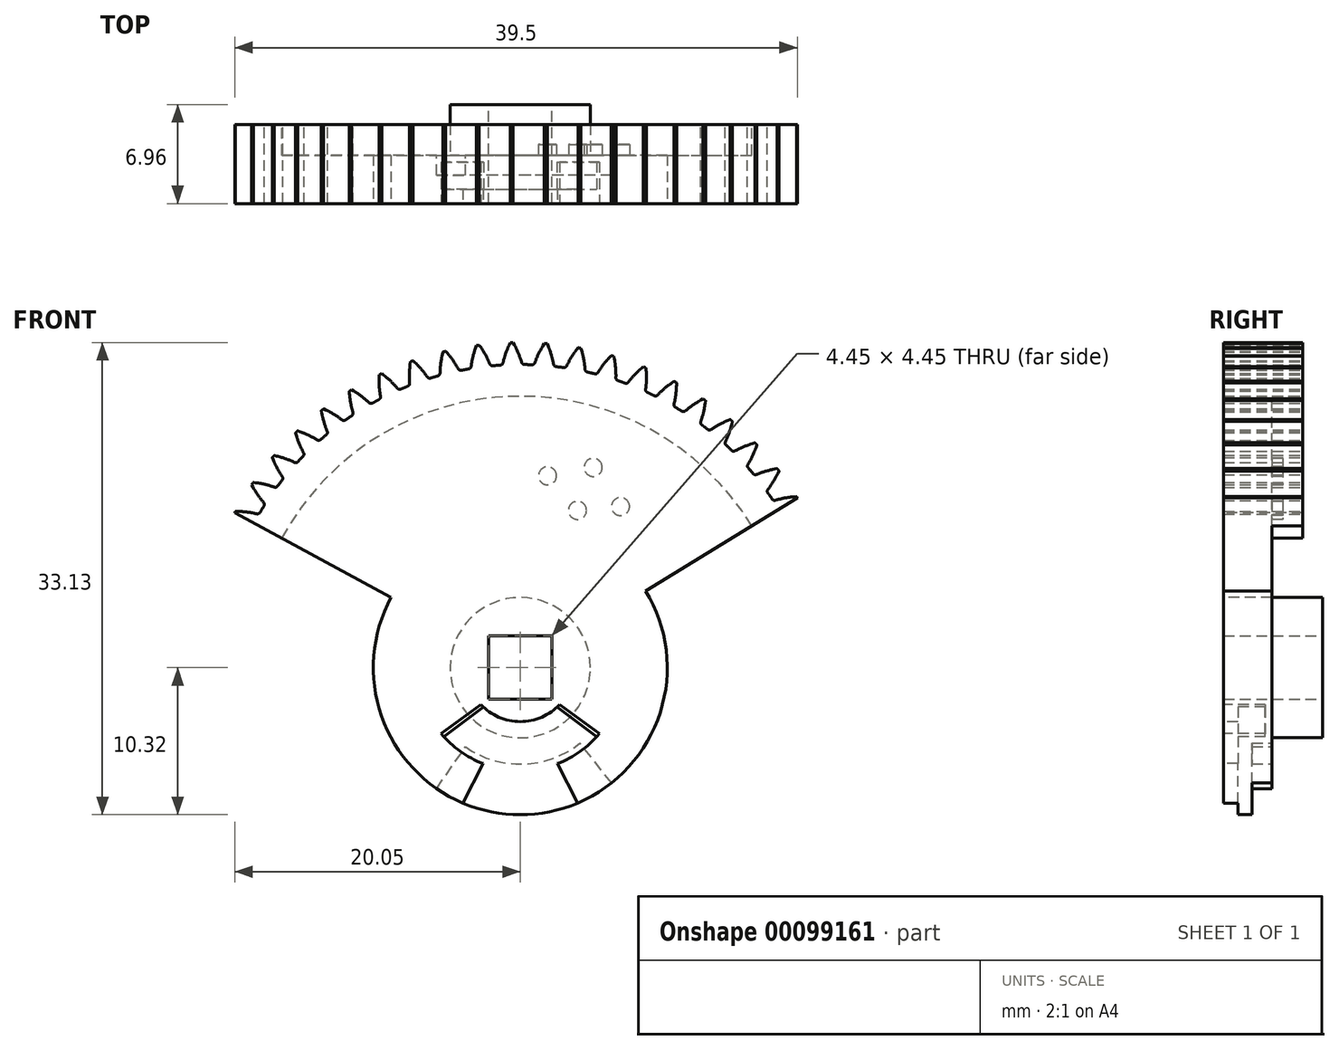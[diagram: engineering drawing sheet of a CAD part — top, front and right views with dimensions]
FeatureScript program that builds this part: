
annotation { "Feature Type Name" : "Feature", "Feature Type Description" : "" }
export const myFeature = defineFeature(function(context is Context, id is Id, definition is map)
    precondition{}
    {
        {
            assignVariable(context, id + "F0", {"name" : "Teeth", "anyValue" : 60});
        }
        {
            var Q0;
            Q0=qCreatedBy(makeId("Front.planeOp"),FACE);
            var sketch = newSketch(context, id + "F1", { "sketchPlane" : qUnion([Q0])});
            skCircle(sketch, "E0", {"center": v(0, 0) * mm, "radius": 20.77 * mm, "construction": true});
            skLineSegment(sketch, "E1", {"start": v(0, 0) * mm, "end": v(-0.74, 20.75) * mm, "construction": true});
            skLineSegment(sketch, "E2", {"start": v(0, 0) * mm, "end": v(-1.69, 20.7) * mm, "construction": true});
            skLineSegment(sketch, "E3", {"start": v(0, 0) * mm, "end": v(-2.64, 20.6) * mm, "construction": true});
            skLineSegment(sketch, "E4", {"start": v(-2.64, 20.6) * mm, "end": v(0.2, 20.96) * mm, "construction": true});
            skLineSegment(sketch, "E5", {"start": v(0, 0) * mm, "end": v(-3.58, 20.45) * mm, "construction": true});
            skLineSegment(sketch, "E6", {"start": v(-3.58, 20.45) * mm, "end": v(0.17, 21.11) * mm, "construction": true});
            skLineSegment(sketch, "E7", {"start": v(-2.64, 20.6) * mm, "end": v(-1.69, 20.7) * mm, "construction": true});
            skLineSegment(sketch, "E8", {"start": v(-3.58, 20.45) * mm, "end": v(-2.64, 20.6) * mm, "construction": true});
            skLineSegment(sketch, "E9", {"start": v(-2.64, 20.6) * mm, "end": v(-0.74, 20.75) * mm, "construction": true});
            skLineSegment(sketch, "E10", {"start": v(-3.58, 20.45) * mm, "end": v(-0.74, 20.75) * mm, "construction": true});
            skLineSegment(sketch, "E11", {"start": v(0, 0) * mm, "end": v(-6.35, 19.77) * mm, "construction": true});
            skLineSegment(sketch, "E12", {"start": v(-6.35, 19.77) * mm, "end": v(-0.03, 21.8) * mm, "construction": true});
            skLineSegment(sketch, "E13", {"start": v(0, 0) * mm, "end": v(-5.44, 20.04) * mm, "construction": true});
            skLineSegment(sketch, "E14", {"start": v(-5.44, 20.04) * mm, "end": v(0.06, 21.53) * mm, "construction": true});
            skLineSegment(sketch, "E15", {"start": v(0, 0) * mm, "end": v(-4.51, 20.27) * mm, "construction": true});
            skLineSegment(sketch, "E16", {"start": v(-4.51, 20.27) * mm, "end": v(0.13, 21.3) * mm, "construction": true});
            skLineSegment(sketch, "E17", {"start": v(-4.51, 20.27) * mm, "end": v(-3.58, 20.45) * mm, "construction": true});
            skLineSegment(sketch, "E18", {"start": v(-4.51, 20.27) * mm, "end": v(-5.44, 20.04) * mm, "construction": true});
            skLineSegment(sketch, "E19", {"start": v(-5.44, 20.04) * mm, "end": v(-6.35, 19.77) * mm, "construction": true});
            skLineSegment(sketch, "E20", {"start": v(-4.51, 20.27) * mm, "end": v(-0.74, 20.75) * mm, "construction": true});
            skLineSegment(sketch, "E21", {"start": v(-5.44, 20.04) * mm, "end": v(-0.74, 20.75) * mm, "construction": true});
            skLineSegment(sketch, "E22", {"start": v(-6.35, 19.77) * mm, "end": v(-0.74, 20.75) * mm, "construction": true});
            skLineSegment(sketch, "E23", {"start": v(0, 0) * mm, "end": v(-8.13, 19.1) * mm, "construction": true});
            skLineSegment(sketch, "E24", {"start": v(-8.13, 19.1) * mm, "end": v(-0.3, 22.44) * mm, "construction": true});
            skLineSegment(sketch, "E25", {"start": v(0, 0) * mm, "end": v(-9, 18.71) * mm, "construction": true});
            skLineSegment(sketch, "E26", {"start": v(-9, 18.71) * mm, "end": v(-0.5, 22.8) * mm, "construction": true});
            skLineSegment(sketch, "E27", {"start": v(0, 0) * mm, "end": v(-9.85, 18.28) * mm, "construction": true});
            skLineSegment(sketch, "E28", {"start": v(0, 0) * mm, "end": v(-7.25, 19.46) * mm, "construction": true});
            skLineSegment(sketch, "E29", {"start": v(-7.25, 19.46) * mm, "end": v(-0.15, 22.1) * mm, "construction": true});
            skLineSegment(sketch, "E30", {"start": v(-6.35, 19.77) * mm, "end": v(-7.25, 19.46) * mm, "construction": true});
            skLineSegment(sketch, "E31", {"start": v(-7.25, 19.46) * mm, "end": v(-8.13, 19.1) * mm, "construction": true});
            skLineSegment(sketch, "E32", {"start": v(-8.13, 19.1) * mm, "end": v(-9, 18.71) * mm, "construction": true});
            skLineSegment(sketch, "E33", {"start": v(-9, 18.71) * mm, "end": v(-9.85, 18.28) * mm, "construction": true});
            skLineSegment(sketch, "E34", {"start": v(-0.74, 20.75) * mm, "end": v(-7.25, 19.46) * mm, "construction": true});
            skLineSegment(sketch, "E35", {"start": v(-0.74, 20.75) * mm, "end": v(-8.13, 19.1) * mm, "construction": true});
            skLineSegment(sketch, "E36", {"start": v(-0.74, 20.75) * mm, "end": v(-9, 18.71) * mm, "construction": true});
            skLineSegment(sketch, "E37", {"start": v(-0.74, 20.75) * mm, "end": v(-9.85, 18.28) * mm, "construction": true});
            skCircle(sketch, "E38", {"center": v(0, 0) * mm, "radius": 22.1 * mm, "construction": true});
            skCircle(sketch, "E39", {"center": v(0, 0) * mm, "radius": 22.81 * mm});
            skPoint(sketch, "E40", {"position": v(0, 22.1) * mm});
            skLineSegment(sketch, "E41", {"start": v(0, 0) * mm, "end": v(-0.23, 8.6) * mm, "construction": true});
            skPoint(sketch, "E42.MirrorP", {"position": v(-1.16, 22.07) * mm});
            skLineSegment(sketch, "E43", {"start": v(-1.16, 22.07) * mm, "end": v(0, 0) * mm, "construction": true});
            skLineSegment(sketch, "E44", {"start": v(0, 0) * mm, "end": v(0, 22.1) * mm, "construction": true});
            skLineSegment(sketch, "E45", {"start": v(-1.69, 20.7) * mm, "end": v(-0.74, 20.75) * mm, "construction": true});
            skLineSegment(sketch, "E46", {"start": v(0.2, 20.96) * mm, "end": v(0.17, 21.11) * mm, "construction": true});
            skLineSegment(sketch, "E47", {"start": v(0, 0) * mm, "end": v(0, 10.19) * mm, "construction": true});
            skCircle(sketch, "E48", {"center": v(0, 0) * mm, "radius": 21.27 * mm});
            skSolve(sketch);
        }
        {
            var Q0;
            Q0=qCreatedBy(makeId("Front.planeOp"),FACE);
            var sketch = newSketch(context, id + "F2", { "sketchPlane" : qUnion([Q0])});
            skCircle(sketch, "E49.0", {"center": v(0, 0) * mm, "radius": 22.1 * mm, "construction": true});
            skPoint(sketch, "E50.0", {"position": v(-0.5, 22.8) * mm});
            skPoint(sketch, "E50.1", {"position": v(-0.3, 22.44) * mm});
            skPoint(sketch, "E50.2", {"position": v(-0.15, 22.1) * mm});
            skPoint(sketch, "E50.3", {"position": v(-0.03, 21.8) * mm});
            skPoint(sketch, "E50.4", {"position": v(0.06, 21.53) * mm});
            skPoint(sketch, "E50.6", {"position": v(0.17, 21.11) * mm});
            skPoint(sketch, "E50.7", {"position": v(0.2, 20.96) * mm});
            skPoint(sketch, "E50.8", {"position": v(0.13, 21.3) * mm});
            skLineSegment(sketch, "E51.0", {"start": v(0, 0) * mm, "end": v(-0.23, 8.6) * mm, "construction": true});
            skFitSpline(sketch, "E52", {"points": [v(-0.5, 22.8) * mm, v(-0.3, 22.44) * mm, v(-0.15, 22.1) * mm, v(-0.03, 21.8) * mm, v(0.06, 21.53) * mm, v(0.13, 21.3) * mm, v(0.17, 21.11) * mm, v(0.2, 20.96) * mm], "startDerivative": vector(3.27, -6.28) * mm, "endDerivative": vector(0.74, -4.25) * mm});
            skFitSpline(sketch, "E53.MirrorCS", {"points": [v(-0.7, 22.8) * mm, v(-0.87, 22.43) * mm, v(-1, 22.08) * mm, v(-1.11, 21.77) * mm, v(-1.19, 21.5) * mm, v(-1.24, 21.27) * mm, v(-1.28, 21.07) * mm, v(-1.3, 20.92) * mm], "startDerivative": vector(-2.94, -6.45) * mm, "endDerivative": vector(-0.51, -4.28) * mm});
            skCircle(sketch, "E54", {"center": v(0, 0) * mm, "radius": 2.22 * mm});
            skCircle(sketch, "E55.0", {"center": v(0, 0) * mm, "radius": 21.27 * mm});
            skArc(sketch, "E56", {"start": v(-0.5, 22.8) * mm, "mid": v(-0.6, 22.8) * mm, "end": v(-0.7, 22.8) * mm});
            skLineSegment(sketch, "E57", {"start": v(-1.3, 20.92) * mm, "end": v(0, 0) * mm});
            skLineSegment(sketch, "E58", {"start": v(0, 0) * mm, "end": v(0.2, 20.96) * mm});
            skSolve(sketch);
        }
        {
            var Q0;
            {var subQ1=sQuery(id+"F2.wireOp",EDGE,"E52");var subQ9=sQuery(id+"F2.wireOp",EDGE,"rA0usyOi-Jm6w-jZNR-JSDv-ujEcH4bsm2Ol");var subQ11=makeQuery(id+"F2.imprint","INTERSECT",VERTEX,{"derivedFrom":[subQ1,subQ9]});Q0=makeQuery(id+"F2.imprint","IMPRINT",FACE,{"disambiguationData":[TD([[makeQuery(id+"F2.imprint","IMPRINT",EDGE,{"disambiguationData":[TD([[subQ11,1.0]])],"derivedFrom":subQ1}),-1.0]])]});}
            var Q1;
            {var subQ0=sQuery(id+"F2.wireOp",EDGE,"QqPcIgQ4-TZE6-73E5-WQaq-ugCT5JtziKyn");var subQ1=sQuery(id+"F2.wireOp",EDGE,"90be38e0-c88f-493d-85a8-1201295b9109.0");var subQ2=makeQuery(id+"F2.imprint","INTERSECT",VERTEX,{"derivedFrom":[subQ1,subQ0]});Q1=makeQuery(id+"F2.imprint","IMPRINT",FACE,{"disambiguationData":[TD([[makeQuery(id+"F2.imprint","IMPRINT",EDGE,{"disambiguationData":[TD([[subQ2,1.0]])],"derivedFrom":subQ1}),1.0]])]});}
            var Q2;
            {var subQ0=sQuery(id+"F2.wireOp",EDGE,"QqPcIgQ4-TZE6-73E5-WQaq-ugCT5JtziKyn");var subQ1=sQuery(id+"F2.wireOp",EDGE,"90be38e0-c88f-493d-85a8-1201295b9109.0");var subQ2=makeQuery(id+"F2.imprint","INTERSECT",VERTEX,{"derivedFrom":[subQ1,subQ0]});Q2=makeQuery(id+"F2.imprint","IMPRINT",FACE,{"disambiguationData":[TD([[makeQuery(id+"F2.imprint","IMPRINT",EDGE,{"disambiguationData":[TD([[subQ2,-1.0]])],"derivedFrom":subQ1}),1.0]])]});}
            var Q3;
            {var subQ1=sQuery(id+"F2.wireOp",EDGE,"E52");var subQ8=sQuery(id+"F2.wireOp",EDGE,"b861a5ab-cd51-40f1-92ab-cea0f5fe0d4d.1");var subQ11=makeQuery(id+"F2.imprint","INTERSECT",VERTEX,{"derivedFrom":[subQ1,subQ8]});Q3=makeQuery(id+"F2.imprint","IMPRINT",FACE,{"disambiguationData":[TD([[makeQuery(id+"F2.imprint","IMPRINT",EDGE,{"disambiguationData":[TD([[subQ11,1.0]])],"derivedFrom":subQ1}),-1.0]])]});}
            var Q4;
            {var subQ0=sQuery(id+"F2.wireOp",EDGE,"b861a5ab-cd51-40f1-92ab-cea0f5fe0d4d.0");var subQ1=sQuery(id+"F2.wireOp",EDGE,"E54");var subQ2=makeQuery(id+"F2.imprint","INTERSECT",VERTEX,{"derivedFrom":[subQ1,subQ0]});Q4=makeQuery(id+"F2.imprint","IMPRINT",FACE,{"disambiguationData":[TD([[makeQuery(id+"F2.imprint","IMPRINT",EDGE,{"disambiguationData":[TD([[subQ2,-1.0]])],"derivedFrom":subQ1}),-1.0]])]});}
            var Q5;
            {var subQ0=sQuery(id+"F2.wireOp",EDGE,"b861a5ab-cd51-40f1-92ab-cea0f5fe0d4d.0");var subQ1=sQuery(id+"F2.wireOp",EDGE,"E54");var subQ2=makeQuery(id+"F2.imprint","INTERSECT",VERTEX,{"derivedFrom":[subQ1,subQ0]});Q5=makeQuery(id+"F2.imprint","IMPRINT",FACE,{"disambiguationData":[TD([[makeQuery(id+"F2.imprint","IMPRINT",EDGE,{"disambiguationData":[TD([[subQ2,1.0]])],"derivedFrom":subQ1}),-1.0]])]});}
            extrude(context, id + "F3", {"entities" : qUnion([Q0, Q1, Q2, Q3, Q4, Q5]), "depth" : 5.56 * mm});
        }
        {
            var Q0;
            Q0=makeQuery(id+"F3.opExtrude","SWEPT_EDGE",EDGE,{"disambiguationData":[OSD([sQuery(id+"F2.wireOp",EDGE,"b861a5ab-cd51-40f1-92ab-cea0f5fe0d4d.1"),sQuery(id+"F2.wireOp",EDGE,"E55.0")])]});
            var Q1;
            Q1=makeQuery(id+"F3.opExtrude","SWEPT_EDGE",EDGE,{"disambiguationData":[OSD([sQuery(id+"F2.wireOp",EDGE,"b861a5ab-cd51-40f1-92ab-cea0f5fe0d4d.0"),sQuery(id+"F2.wireOp",EDGE,"E55.0")])]});
            fillet(context, id + "F4", {"entities" : qUnion([Q0, Q1]), "radius" : 0.2 * mm, "tangentPropagation" : true, "allowEdgeOverflow" : false});
        }
        {
            var Q0;
            Q0=makeQuery(id+"F4.opFillet","BLEND_FACE",FACE,{"disambiguationData":[OSD([sQuery(id+"F2.wireOp",EDGE,"E55.0"),sQuery(id+"F2.wireOp",EDGE,"E57")])]});
            var Q1;
            Q1=makeQuery(id+"F3.opExtrude","SWEPT_FACE",FACE,{"disambiguationData":[OSD([sQuery(id+"F2.wireOp",EDGE,"E57")])]});
            var Q2;
            Q2=makeQuery(id+"F3.opExtrude","SWEPT_FACE",FACE,{"disambiguationData":[OSD([sQuery(id+"F2.wireOp",EDGE,"E53.MirrorCS")])]});
            var Q3;
            Q3=makeQuery(id+"F3.opExtrude","SWEPT_FACE",FACE,{"disambiguationData":[OSD([sQuery(id+"F2.wireOp",EDGE,"E56")])]});
            var Q4;
            Q4=makeQuery(id+"F3.opExtrude","SWEPT_FACE",FACE,{"disambiguationData":[OSD([sQuery(id+"F2.wireOp",EDGE,"E52")])]});
            var Q5;
            Q5=makeQuery(id+"F3.opExtrude","SWEPT_FACE",FACE,{"disambiguationData":[OSD([sQuery(id+"F2.wireOp",EDGE,"E58")])]});
            var Q6;
            Q6=makeQuery(id+"F4.opFillet","BLEND_FACE",FACE,{"disambiguationData":[OSD([sQuery(id+"F2.wireOp",EDGE,"E55.0"),sQuery(id+"F2.wireOp",EDGE,"E58")])]});
            var Q7;
            Q7=makeQuery(id+"F3.opExtrude","SWEPT_FACE",FACE,{"disambiguationData":[OSD([sQuery(id+"F2.wireOp",EDGE,"E55.0")])]});
            circularPattern(context, id + "F5", {"faces" : qUnion([Q0, Q1, Q2, Q3, Q4, Q5, Q6]), "axis" : qUnion([Q7]), "angle" : 360 * degree, "instanceCount" : round(getVariable(context, 'Teeth')), "equalSpace" : true, "patternType" : PatternType.FACE});
        }
        {
            var Q0;
            Q0=makeQuery(id+"F3.opExtrude","CAP_FACE",FACE,{"disambiguationData":[OSD([sQuery(id+"F2.wireOp",EDGE,"E52"),sQuery(id+"F2.wireOp",EDGE,"E53.MirrorCS"),sQuery(id+"F2.wireOp",EDGE,"E54"),sQuery(id+"F2.wireOp",EDGE,"E55.0"),sQuery(id+"F2.wireOp",EDGE,"E56")])],"isStart":false});
            var sketch = newSketch(context, id + "F6", { "sketchPlane" : qUnion([Q0])});
            skLineSegment(sketch, "E59", {"start": v(-9.07, 4.92) * mm, "end": v(-20.05, 10.88) * mm});
            skLineSegment(sketch, "E60", {"start": v(-25.13, -0.66) * mm, "end": v(29.24, 0.77) * mm, "construction": true});
            skLineSegment(sketch, "E61", {"start": v(0, 0) * mm, "end": v(-0.25, 9.5) * mm, "construction": true});
            skLineSegment(sketch, "E62.MirrorCS", {"start": v(8.8, 5.4) * mm, "end": v(19.45, 11.92) * mm});
            skArc(sketch, "E63", {"start": v(-9.07, 4.92) * mm, "mid": v(0.27, -10.32) * mm, "end": v(8.8, 5.4) * mm});
            skArc(sketch, "E64", {"start": v(-20.05, 10.88) * mm, "mid": v(0.6, -22.8) * mm, "end": v(19.45, 11.92) * mm});
            skSolve(sketch);
        }
        {
            var Q0;
            Q0 = qSketchRegion(id + "F6", true);
            extrude(context, id + "F7", {"entities" : qUnion([Q0]), "operationType" : NewBodyOperationType.REMOVE, "oppositeDirection" : true, "depth" : 25.4 * mm});
        }
        {
            var Q0;
            Q0=makeQuery(id+"F3.opExtrude","CAP_FACE",FACE,{"disambiguationData":[OSD([sQuery(id+"F2.wireOp",EDGE,"E52"),sQuery(id+"F2.wireOp",EDGE,"E53.MirrorCS"),sQuery(id+"F2.wireOp",EDGE,"E54"),sQuery(id+"F2.wireOp",EDGE,"E55.0"),sQuery(id+"F2.wireOp",EDGE,"E56")])],"isStart":false});
            var sketch = newSketch(context, id + "F8", { "sketchPlane" : qUnion([Q0])});
            skArc(sketch, "E65", {"start": v(-2.77, -2.58) * mm, "mid": v(-1.51, -3.47) * mm, "end": v(0, -3.78) * mm});
            skLineSegment(sketch, "E66", {"start": v(0, -3.78) * mm, "end": v(0, -10.32) * mm, "construction": true});
            skLineSegment(sketch, "E67", {"start": v(-4.03, -9.5) * mm, "end": v(-2.62, -6.74) * mm});
            skLineSegment(sketch, "E68", {"start": v(0, -4.63) * mm, "end": v(-5.54, -4.63) * mm, "construction": true});
            skArc(sketch, "E69", {"start": v(-5.54, -4.63) * mm, "mid": v(-4.21, -5.87) * mm, "end": v(-2.62, -6.74) * mm});
            skLineSegment(sketch, "E70", {"start": v(-5.54, -4.63) * mm, "end": v(-2.77, -2.58) * mm});
            skArc(sketch, "E71", {"start": v(-4.03, -9.5) * mm, "mid": v(-2.06, -10.11) * mm, "end": v(0, -10.32) * mm});
            skArc(sketch, "E72.MirrorCS", {"start": v(2.77, -2.58) * mm, "mid": v(1.51, -3.47) * mm, "end": v(0, -3.78) * mm});
            skLineSegment(sketch, "E73.MirrorCS", {"start": v(5.54, -4.63) * mm, "end": v(2.77, -2.58) * mm});
            skArc(sketch, "E74.MirrorCS", {"start": v(5.54, -4.63) * mm, "mid": v(4.21, -5.87) * mm, "end": v(2.62, -6.74) * mm});
            skLineSegment(sketch, "E75.MirrorCS", {"start": v(4.03, -9.5) * mm, "end": v(2.62, -6.74) * mm});
            skArc(sketch, "E76.MirrorCS", {"start": v(4.03, -9.5) * mm, "mid": v(2.06, -10.11) * mm, "end": v(0, -10.32) * mm});
            skSolve(sketch);
        }
        {
            var Q0;
            Q0 = qSketchRegion(id + "F8", true);
            extrude(context, id + "F9", {"entities" : qUnion([Q0]), "operationType" : NewBodyOperationType.REMOVE, "flatOperationType" : FlatOperationType.REMOVE, "oppositeDirection" : true, "offsetDistance" : 25.4 * mm, "depth" : 1.02 * mm, "domain" : OperationDomain.MODEL});
        }
        {
            var Q0;
            Q0=makeQuery(id+"F9.boolean.opBoolean","COPY",FACE,{"derivedFrom":makeQuery(id+"F9.opExtrude","CAP_FACE",FACE,{"disambiguationData":[OSD([sQuery(id+"F8.wireOp",EDGE,"7rp70U2j-1LJA-0Fld-UV0Z-6pLJ0CQ2ZY8P"),sQuery(id+"F8.wireOp",EDGE,"ceQvra0M-UReR-jHEd-x8fO-Yybck840S4PW"),sQuery(id+"F8.wireOp",EDGE,"0Ofc3ZeZ-KIVS-80YM-w8vh-BZbH9Hb7MnxD"),sQuery(id+"F8.wireOp",EDGE,"TCcQ6ZID-ELh7-HWsc-UNgQ-hA6RSax0RGy1"),sQuery(id+"F8.wireOp",EDGE,"E65"),sQuery(id+"F8.wireOp",EDGE,"881be9a5-07b3-4436-9b2d-f41688641e410.MirrorCS"),sQuery(id+"F8.wireOp",EDGE,"60d219b5-2a95-409c-85be-067e802003850.MirrorCS"),sQuery(id+"F8.wireOp",EDGE,"41792c79-b3ff-4013-8b71-ca6652491c0a0.MirrorCS"),sQuery(id+"F8.wireOp",EDGE,"9388b70a-ac15-4c98-b249-1cef6bb6d7810.MirrorCS")])],"isStart":false})});
            var sketch = newSketch(context, id + "F10", { "sketchPlane" : qUnion([Q0])});
            skLineSegment(sketch, "E77", {"start": v(-2.77, -2.58) * mm, "end": v(-5.54, -4.63) * mm});
            skArc(sketch, "E78", {"start": v(-2.77, -2.58) * mm, "mid": v(-2.68, -2.67) * mm, "end": v(-2.59, -2.76) * mm});
            skArc(sketch, "E79", {"start": v(-5.54, -4.63) * mm, "mid": v(-5.46, -4.73) * mm, "end": v(-5.37, -4.83) * mm});
            skLineSegment(sketch, "E80", {"start": v(-2.59, -2.76) * mm, "end": v(-5.37, -4.83) * mm});
            skLineSegment(sketch, "E81", {"start": v(0, 0) * mm, "end": v(0, -3.78) * mm, "construction": true});
            skArc(sketch, "E82.MirrorCS", {"start": v(2.77, -2.58) * mm, "mid": v(2.68, -2.67) * mm, "end": v(2.59, -2.76) * mm});
            skArc(sketch, "E83.MirrorCS", {"start": v(5.54, -4.63) * mm, "mid": v(5.46, -4.73) * mm, "end": v(5.37, -4.83) * mm});
            skLineSegment(sketch, "E84.MirrorCS", {"start": v(2.77, -2.58) * mm, "end": v(5.54, -4.63) * mm});
            skLineSegment(sketch, "E85.MirrorCS", {"start": v(2.59, -2.76) * mm, "end": v(5.37, -4.83) * mm});
            skSolve(sketch);
        }
        {
            var Q0;
            Q0 = qSketchRegion(id + "F10", true);
            extrude(context, id + "F11", {"entities" : qUnion([Q0]), "operationType" : NewBodyOperationType.REMOVE, "oppositeDirection" : true, "depth" : 1.9 * mm});
        }
        {
            var Q0;
            Q0=makeQuery(id+"F3.opExtrude","CAP_FACE",FACE,{"disambiguationData":[OSD([sQuery(id+"F2.wireOp",EDGE,"E52"),sQuery(id+"F2.wireOp",EDGE,"E53.MirrorCS"),sQuery(id+"F2.wireOp",EDGE,"E54"),sQuery(id+"F2.wireOp",EDGE,"E55.0"),sQuery(id+"F2.wireOp",EDGE,"E56")])],"isStart":true});
            var sketch = newSketch(context, id + "F12", { "sketchPlane" : qUnion([Q0])});
            skCircle(sketch, "E86", {"center": v(0, 0) * mm, "radius": 19.05 * mm});
            skSolve(sketch);
        }
        {
            var Q0;
            Q0 = qSketchRegion(id + "F12", true);
            extrude(context, id + "F13", {"entities" : qUnion([Q0]), "operationType" : NewBodyOperationType.REMOVE, "oppositeDirection" : true, "depth" : 2.16 * mm});
        }
        {
            var Q0;
            Q0=makeQuery(id+"F13.boolean.opBoolean","COPY",FACE,{"derivedFrom":makeQuery(id+"F13.opExtrude","CAP_FACE",FACE,{"disambiguationData":[OSD([sQuery(id+"F12.wireOp",EDGE,"E86")])],"isStart":false})});
            var sketch = newSketch(context, id + "F14", { "sketchPlane" : qUnion([Q0])});
            skPoint(sketch, "E87.endSnap0", {"position": v(-0.27, -10.32) * mm});
            skLineSegment(sketch, "E88", {"start": v(-0.27, -10.32) * mm, "end": v(-6.46, -10.15) * mm, "construction": true});
            skLineSegment(sketch, "E89", {"start": v(-6.46, -10.15) * mm, "end": v(-6.4, -8.1) * mm, "construction": true});
            skLineSegment(sketch, "E90", {"start": v(-6.4, -8.1) * mm, "end": v(-4.2, -5.3) * mm});
            skLineSegment(sketch, "E91", {"start": v(-0.27, -10.32) * mm, "end": v(-0.27, -6.76) * mm, "construction": true});
            skArc(sketch, "E92", {"start": v(-4.2, -5.3) * mm, "mid": v(-0.22, -6.76) * mm, "end": v(3.85, -5.56) * mm});
            skArc(sketch, "E93", {"start": v(-6.4, -8.1) * mm, "mid": v(-0.33, -10.31) * mm, "end": v(5.88, -8.48) * mm});
            skLineSegment(sketch, "E94.MirrorCS", {"start": v(-0.27, -10.32) * mm, "end": v(5.92, -10.15) * mm, "construction": true});
            skLineSegment(sketch, "E95", {"start": v(5.92, -10.15) * mm, "end": v(5.88, -8.48) * mm, "construction": true});
            skLineSegment(sketch, "E96", {"start": v(5.88, -8.48) * mm, "end": v(3.85, -5.56) * mm});
            skSolve(sketch);
        }
        {
            var Q0;
            Q0=makeQuery(id+"F14.imprint","IMPRINT",FACE,{"disambiguationData":[TD([[makeQuery(id+"F14.imprint","IMPRINT",EDGE,{"derivedFrom":sQuery(id+"F14.wireOp",EDGE,"4qyKxU2X-wfWm-waPb-otx4-mvksZVDVlzwU")}),-1.0]])]});
            var Q1;
            Q1=makeQuery(id+"F14.imprint","IMPRINT",FACE,{"disambiguationData":[TD([[makeQuery(id+"F14.imprint","IMPRINT",EDGE,{"derivedFrom":sQuery(id+"F14.wireOp",EDGE,"E90")}),-1.0]])]});
            extrude(context, id + "F15", {"entities" : qUnion([Q0, Q1]), "operationType" : NewBodyOperationType.REMOVE, "oppositeDirection" : true, "depth" : 1.4 * mm});
        }
        {
            var Q0;
            Q0=makeQuery(id+"F13.boolean.opBoolean","COPY",FACE,{"derivedFrom":makeQuery(id+"F13.opExtrude","CAP_FACE",FACE,{"disambiguationData":[OSD([sQuery(id+"F12.wireOp",EDGE,"E86")])],"isStart":false})});
            var sketch = newSketch(context, id + "F16", { "sketchPlane" : qUnion([Q0])});
            skCircle(sketch, "E97", {"center": v(0, 0) * mm, "radius": 4.92 * mm});
            skSolve(sketch);
        }
        {
            var Q0;
            Q0 = qSketchRegion(id + "F16", true);
            extrude(context, id + "F17", {"entities" : qUnion([Q0]), "operationType" : NewBodyOperationType.ADD, "depth" : 3.56 * mm});
        }
        {
            var Q0;
            Q0=makeQuery(id+"F17.opExtrude","CAP_FACE",FACE,{"disambiguationData":[OSD([sQuery(id+"F16.wireOp",EDGE,"E97")])],"isStart":false});
            var sketch = newSketch(context, id + "F18", { "sketchPlane" : qUnion([Q0])});
            skLineSegment(sketch, "E98.bottom", {"start": v(2.22, 2.22) * mm, "end": v(-2.22, 2.22) * mm});
            skLineSegment(sketch, "E98.top", {"start": v(2.22, -2.22) * mm, "end": v(-2.22, -2.22) * mm});
            skLineSegment(sketch, "E98.left", {"start": v(2.22, 2.22) * mm, "end": v(2.22, -2.22) * mm});
            skLineSegment(sketch, "E98.right", {"start": v(-2.22, 2.22) * mm, "end": v(-2.22, -2.22) * mm});
            skPoint(sketch, "E98.middle", {"position": v(0, 0) * mm});
            skSolve(sketch);
        }
        {
            var Q0;
            Q0 = qSketchRegion(id + "F18", true);
            extrude(context, id + "F19", {"entities" : qUnion([Q0]), "operationType" : NewBodyOperationType.REMOVE, "endBound" : BoundingType.THROUGH_ALL, "oppositeDirection" : true, "depth" : 25.4 * mm});
        }
        {
            var Q0;
            Q0=makeQuery(id+"F13.boolean.opBoolean","COPY",FACE,{"derivedFrom":makeQuery(id+"F13.opExtrude","CAP_FACE",FACE,{"disambiguationData":[OSD([sQuery(id+"F12.wireOp",EDGE,"E86")])],"isStart":false})});
            var sketch = newSketch(context, id + "F20", { "sketchPlane" : qUnion([Q0])});
            skLineSegment(sketch, "E99", {"start": v(0, 0) * mm, "end": v(-14.07, 0) * mm, "construction": true});
            skLineSegment(sketch, "E100", {"start": v(0, 0) * mm, "end": v(-7.87, 21.62) * mm, "construction": true});
            skLineSegment(sketch, "E101", {"start": v(0, 0) * mm, "end": v(-4.02, 11.04) * mm, "construction": true});
            skCircle(sketch, "E102", {"center": v(-4.02, 11.04) * mm, "radius": 0.64 * mm});
            skCircle(sketch, "E103", {"center": v(-5.11, 14.05) * mm, "radius": 0.64 * mm});
            skLineSegment(sketch, "E104", {"start": v(-4.55, 12.5) * mm, "end": v(-2.5, 13.24) * mm, "construction": true});
            skLineSegment(sketch, "E105", {"start": v(-2.5, 13.24) * mm, "end": v(-1.91, 13.46) * mm, "construction": true});
            skCircle(sketch, "E106", {"center": v(-1.91, 13.46) * mm, "radius": 0.63 * mm});
            skLineSegment(sketch, "E107", {"start": v(-4.02, 11.04) * mm, "end": v(-4.55, 12.5) * mm, "construction": true});
            skLineSegment(sketch, "E108", {"start": v(0, 0) * mm, "end": v(-7.19, 11.54) * mm, "construction": true});
            skCircle(sketch, "E109", {"center": v(-7.04, 11.3) * mm, "radius": 0.64 * mm});
            skSolve(sketch);
        }
        {
            var Q0;
            Q0=makeQuery(id+"F20.imprint","IMPRINT",FACE,{"disambiguationData":[TD([[makeQuery(id+"F20.imprint","IMPRINT",EDGE,{"derivedFrom":sQuery(id+"F20.wireOp",EDGE,"d775f8e6-8f77-4304-8d53-d1d3162926350.MirrorC")}),-1.0]])]});
            var Q1;
            Q1=makeQuery(id+"F20.imprint","IMPRINT",FACE,{"disambiguationData":[TD([[makeQuery(id+"F20.imprint","IMPRINT",EDGE,{"derivedFrom":sQuery(id+"F20.wireOp",EDGE,"E103")}),1.0]])]});
            var Q2;
            Q2=makeQuery(id+"F20.imprint","IMPRINT",FACE,{"disambiguationData":[TD([[makeQuery(id+"F20.imprint","IMPRINT",EDGE,{"derivedFrom":sQuery(id+"F20.wireOp",EDGE,"E102")}),1.0]])]});
            var Q3;
            Q3=makeQuery(id+"F20.imprint","IMPRINT",FACE,{"disambiguationData":[TD([[makeQuery(id+"F20.imprint","IMPRINT",EDGE,{"derivedFrom":sQuery(id+"F20.wireOp",EDGE,"u67YAFrJ-qeJw-izZR-xDkX-8DxLixYBhPkI")}),1.0]])]});
            var Q4;
            Q4=makeQuery(id+"F20.imprint","IMPRINT",FACE,{"disambiguationData":[TD([[makeQuery(id+"F20.imprint","IMPRINT",EDGE,{"derivedFrom":sQuery(id+"F20.wireOp",EDGE,"d7813c1b-9fb1-42ca-9f87-8bef3b6593eb0.MirrorC")}),-1.0]])]});
            var Q5;
            Q5=makeQuery(id+"F20.imprint","IMPRINT",FACE,{"disambiguationData":[TD([[makeQuery(id+"F20.imprint","IMPRINT",EDGE,{"derivedFrom":sQuery(id+"F20.wireOp",EDGE,"E106")}),1.0]])]});
            var Q6;
            Q6=makeQuery(id+"F20.imprint","IMPRINT",FACE,{"disambiguationData":[TD([[makeQuery(id+"F20.imprint","IMPRINT",EDGE,{"derivedFrom":sQuery(id+"F20.wireOp",EDGE,"E109")}),1.0]])]});
            var Q7;
            Q7=sQuery(id+"F20.wireOp",EDGE,"d775f8e6-8f77-4304-8d53-d1d3162926350.MirrorC");
            var Q8;
            Q8=sQuery(id+"F20.wireOp",EDGE,"E103");
            var Q9;
            Q9=sQuery(id+"F20.wireOp",EDGE,"u67YAFrJ-qeJw-izZR-xDkX-8DxLixYBhPkI");
            var Q10;
            Q10=sQuery(id+"F20.wireOp",EDGE,"E102");
            extrude(context, id + "F21", {"entities" : qUnion([Q0, Q1, Q2, Q3, Q4, Q5, Q6]), "operationType" : NewBodyOperationType.ADD, "surfaceEntities" : qUnion([Q7, Q8, Q9, Q10]), "depth" : 0.76 * mm});
        }
    });
